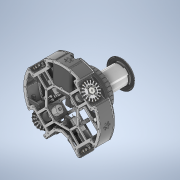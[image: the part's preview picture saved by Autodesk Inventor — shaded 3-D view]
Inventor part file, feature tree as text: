
AUTODESK INVENTOR PART (.ipt)
format: ipt  version: 2020 (Build 240168000, 168)  size: 43,642,880 bytes
history: native  units: mm
features: other x297, mirror x2
ambient origin geometry x8: Origin, YZ Plane, XZ Plane, XY Plane, X Axis, Y Axis, Z Axis, Center Point
bodies: Body1 (feature_tree), Body2 (feature_tree), Body3 (feature_tree), Body4 (feature_tree), Body5 (feature_tree), Body6 (feature_tree), Body7 (feature_tree), Body8 (feature_tree), Body9 (feature_tree), Body10 (feature_tree), Body11 (feature_tree), Body12 (feature_tree), Body13 (feature_tree), Body14 (feature_tree), Body15 (feature_tree), Body16 (feature_tree), Body17 (feature_tree), Body18 (feature_tree), Body19 (feature_tree), Body20 (feature_tree), Body21 (feature_tree), Body22 (feature_tree), Body23 (feature_tree), Body24 (feature_tree), Body25 (feature_tree), Body26 (feature_tree), Body27 (feature_tree), Body28 (feature_tree), Body29 (feature_tree), Body30 (feature_tree), Body31 (feature_tree), Body32 (feature_tree), Body33 (feature_tree), Body34 (feature_tree), Body35 (feature_tree), Body36 (feature_tree), Body37 (feature_tree), Body38 (feature_tree), Body39 (feature_tree), Body40 (feature_tree), Body41 (feature_tree), Body42 (feature_tree), Body43 (feature_tree), Body44 (feature_tree), Body45 (feature_tree), Body46 (feature_tree), Body47 (feature_tree), Body48 (feature_tree), Body49 (feature_tree), Body50 (feature_tree), Body51 (feature_tree), Body52 (feature_tree), Body53 (feature_tree), Body54 (feature_tree), Body55 (feature_tree), Body56 (feature_tree), Body57 (feature_tree), Body58 (feature_tree), Body59 (feature_tree), Body60 (feature_tree), Body61 (feature_tree), Body62 (feature_tree), Body63 (feature_tree), Body64 (feature_tree), Body65 (feature_tree), Body66 (feature_tree), Body67 (feature_tree), Body68 (feature_tree), Body69 (feature_tree), Body70 (feature_tree), Body71 (feature_tree), Body72 (feature_tree), Body73 (feature_tree), Body74 (feature_tree), Body75 (feature_tree), Body76 (feature_tree), Body77 (feature_tree), Body78 (feature_tree), Body79 (feature_tree), Body80 (feature_tree), Body81 (feature_tree), Body82 (feature_tree), Body83 (feature_tree), Body84 (feature_tree), Body85 (feature_tree), Body86 (feature_tree), Body87 (feature_tree), Body88 (feature_tree), Body89 (feature_tree), Body90 (feature_tree), Body91 (feature_tree), Body92 (feature_tree), Body93 (feature_tree), Body94 (feature_tree), Body95 (feature_tree), Body96 (feature_tree), Body97 (feature_tree), Body98 (feature_tree), Body99 (feature_tree), Body100 (feature_tree), Body101 (feature_tree), Body102 (feature_tree), Body103 (feature_tree), Body104 (feature_tree), Body105 (feature_tree), Body106 (feature_tree), Body107 (feature_tree), Body108 (feature_tree), Body109 (feature_tree), Body110 (feature_tree), Body111 (feature_tree), Body112 (feature_tree), Body113 (feature_tree), Body114 (feature_tree), Body115 (feature_tree), Body116 (feature_tree), Body117 (feature_tree), Body118 (feature_tree), Body119 (feature_tree), Body120 (feature_tree), Body121 (feature_tree), Body122 (feature_tree), Body123 (feature_tree), Body124 (feature_tree), Body125 (feature_tree), Body126 (feature_tree), Body127 (feature_tree), Body128 (feature_tree), Body129 (feature_tree), Body130 (feature_tree), Body131 (feature_tree), Body132 (feature_tree), Body133 (feature_tree), Body134 (feature_tree), Body135 (feature_tree), Body136 (feature_tree), Body137 (feature_tree), Body138 (feature_tree), Body139 (feature_tree), Body140 (feature_tree), Body141 (feature_tree), Body142 (feature_tree), Body143 (feature_tree), Body144 (feature_tree), Body145 (feature_tree), Body146 (feature_tree), Body147 (feature_tree), Body148 (feature_tree), Body149 (feature_tree), Body150 (feature_tree), Body151 (feature_tree), Body152 (feature_tree), Body153 (feature_tree), Body154 (feature_tree), Body155 (feature_tree), Body156 (feature_tree), Body157 (feature_tree), Body158 (feature_tree), Body159 (feature_tree), Body160 (feature_tree), Body161 (feature_tree), Body162 (feature_tree), Body163 (feature_tree), Body164 (feature_tree), Body165 (feature_tree), Body166 (feature_tree), Body167 (feature_tree), Body168 (feature_tree), Body169 (feature_tree), Body170 (feature_tree), Body171 (feature_tree), Body172 (feature_tree), Body173 (feature_tree), Body174 (feature_tree), Body175 (feature_tree), Body176 (feature_tree), Body177 (feature_tree), Body178 (feature_tree), Body179 (feature_tree), Body180 (feature_tree), Body181 (feature_tree), Body182 (feature_tree), Body183 (feature_tree), Body184 (feature_tree), Body185 (feature_tree), Body186 (feature_tree), Body187 (feature_tree), Body188 (feature_tree), Body189 (feature_tree), Body190 (feature_tree), Body191 (feature_tree), Body192 (feature_tree), Body193 (feature_tree), Body194 (feature_tree)
feature tree (299):
  other  "main2 render.iam"
  other  "bottom_plate.ipt:1"
  other  "back_motor_short.ipt:1"
  other  "back_motor_short.ipt:2"
  other  "upper_plate.ipt:1"
  other  "9Dof Razor IMU.ipt:1"
  other  "kicker_base_v6_wide.ipt:1"
  other  "kicker_head_flat_v4.ipt:1"
  other  "motor_body.ipt:1"
  other  "motor_body.ipt:2"
  other  "motor_body.ipt:3"
  other  "motor_body.ipt:4"
  other  "GTF Robots 50mm Wheel.ipt:1"
  other  "GTF Robots 50mm Wheel.ipt:2"
  other  "GTF Robots 50mm Wheel.ipt:3"
  other  "GTF Robots 50mm Wheel.ipt:4"
  other  "bat_bed003_clear.ipt:1"
  other  "right_motor_v2.ipt:1"
  other  "tsop_board_black.iam:1::Board.iam:1::Open CASCADE STEP translator 6.8 1.1.1.ipt:1"
  other  "tsop_board_black.iam:1::VCC.iam:1::cdled1608x06g.ipt:1"
  other  "tsop_board_black.iam:1::XP1.iam:1::5822834224.ipt:1"
  other  "tsop_board_black.iam:1::TS32.iam:1::TSOP.ipt:1"
  other  "tsop_board_black.iam:1::TS31.iam:1::TSOP.ipt:1"
  other  "tsop_board_black.iam:1::TS30.iam:1::TSOP.ipt:1"
  other  "tsop_board_black.iam:1::TS29.iam:1::TSOP.ipt:1"
  other  "tsop_board_black.iam:1::TS28.iam:1::TSOP.ipt:1"
  other  "tsop_board_black.iam:1::TS27.iam:1::TSOP.ipt:1"
  other  "tsop_board_black.iam:1::TS26.iam:1::TSOP.ipt:1"
  other  "tsop_board_black.iam:1::TS25.iam:1::TSOP.ipt:1"
  other  "tsop_board_black.iam:1::TS24.iam:1::TSOP.ipt:1"
  other  "tsop_board_black.iam:1::TS23.iam:1::TSOP.ipt:1"
  other  "tsop_board_black.iam:1::TS22.iam:1::TSOP.ipt:1"
  other  "tsop_board_black.iam:1::TS21.iam:1::TSOP.ipt:1"
  other  "tsop_board_black.iam:1::TS20.iam:1::TSOP.ipt:1"
  other  "tsop_board_black.iam:1::TS19.iam:1::TSOP.ipt:1"
  other  "tsop_board_black.iam:1::TS18.iam:1::TSOP.ipt:1"
  other  "tsop_board_black.iam:1::TS17.iam:1::TSOP.ipt:1"
  other  "tsop_board_black.iam:1::TS16.iam:1::TSOP.ipt:1"
  other  "tsop_board_black.iam:1::TS15.iam:1::TSOP.ipt:1"
  other  "tsop_board_black.iam:1::TS14.iam:1::TSOP.ipt:1"
  other  "tsop_board_black.iam:1::TS13.iam:1::TSOP.ipt:1"
  other  "tsop_board_black.iam:1::TS12.iam:1::TSOP.ipt:1"
  other  "tsop_board_black.iam:1::TS11.iam:1::TSOP.ipt:1"
  other  "tsop_board_black.iam:1::TS10.iam:1::TSOP.ipt:1"
  other  "tsop_board_black.iam:1::TS9.iam:1::TSOP.ipt:1"
  other  "tsop_board_black.iam:1::TS8.iam:1::TSOP.ipt:1"
  other  "tsop_board_black.iam:1::TS7.iam:1::TSOP.ipt:1"
  other  "tsop_board_black.iam:1::TS6.iam:1::TSOP.ipt:1"
  other  "tsop_board_black.iam:1::TS5.iam:1::TSOP.ipt:1"
  other  "tsop_board_black.iam:1::TS4.iam:1::TSOP.ipt:1"
  other  "tsop_board_black.iam:1::TS3.iam:1::TSOP.ipt:1"
  other  "tsop_board_black.iam:1::TS2.iam:1::TSOP.ipt:1"
  other  "tsop_board_black.iam:1::TS1.iam:1::TSOP.ipt:1"
  other  "tsop_board_black.iam:1::R33.iam:1::RES0805.ipt:1"
  other  "tsop_board_black.iam:1::MUX2.iam:1::CD74HC4067SM96--3DModel-STEP-56544.ipt:1"
  other  "tsop_board_black.iam:1::MUX1.iam:1::CD74HC4067SM96--3DModel-STEP-56544.ipt:1"
  other  "tsop_board_black.iam:1::C35.iam:1::C0805D(I).ipt:1"
  other  "tsop_board_black.iam:1::C34.iam:1::C0805D(I).ipt:1"
  other  "tsop_board_black.iam:1::C33.iam:1::C0805D(I).ipt:1"
  other  "tsop_board_black.iam:1::C32.iam:1::C0805D(I).ipt:1"
  other  "tsop_board_black.iam:1::C31.iam:1::C0805D(I).ipt:1"
  other  "tsop_board_black.iam:1::C30.iam:1::C0805D(I).ipt:1"
  other  "tsop_board_black.iam:1::C28.iam:1::C0805D(I).ipt:1"
  other  "tsop_board_black.iam:1::C27.iam:1::C0805D(I).ipt:1"
  other  "tsop_board_black.iam:1::C26.iam:1::C0805D(I).ipt:1"
  other  "tsop_board_black.iam:1::C25.iam:1::C0805D(I).ipt:1"
  other  "tsop_board_black.iam:1::C24.iam:1::C0805D(I).ipt:1"
  other  "tsop_board_black.iam:1::C23.iam:1::C0805D(I).ipt:1"
  other  "tsop_board_black.iam:1::C22.iam:1::C0805D(I).ipt:1"
  other  "tsop_board_black.iam:1::C21.iam:1::C0805D(I).ipt:1"
  other  "tsop_board_black.iam:1::C20.iam:1::C0805D(I).ipt:1"
  other  "tsop_board_black.iam:1::C19.iam:1::C0805D(I).ipt:1"
  other  "tsop_board_black.iam:1::C18.iam:1::C0805D(I).ipt:1"
  other  "tsop_board_black.iam:1::C17.iam:1::C0805D(I).ipt:1"
  other  "tsop_board_black.iam:1::C16.iam:1::C0805D(I).ipt:1"
  other  "tsop_board_black.iam:1::C15.iam:1::C0805D(I).ipt:1"
  other  "tsop_board_black.iam:1::C14.iam:1::C0805D(I).ipt:1"
  other  "tsop_board_black.iam:1::C12.iam:1::C0805D(I).ipt:1"
  other  "tsop_board_black.iam:1::C11.iam:1::C0805D(I).ipt:1"
  other  "tsop_board_black.iam:1::C10.iam:1::C0805D(I).ipt:1"
  other  "tsop_board_black.iam:1::C9.iam:1::C0805D(I).ipt:1"
  other  "tsop_board_black.iam:1::C8.iam:1::C0805D(I).ipt:1"
  other  "tsop_board_black.iam:1::C7.iam:1::C0805D(I).ipt:1"
  other  "tsop_board_black.iam:1::C6.iam:1::C0805D(I).ipt:1"
  other  "tsop_board_black.iam:1::C5.iam:1::C0805D(I).ipt:1"
  other  "tsop_board_black.iam:1::C4.iam:1::C0805D(I).ipt:1"
  other  "tsop_board_black.iam:1::C3.iam:1::C0805D(I).ipt:1"
  other  "tsop_board_black.iam:1::C2.iam:1::C0805D(I).ipt:1"
  other  "tsop_board_black.iam:1::C1.iam:1::C0805D(I).ipt:1"
  mirror  "mirror_50.ipt:1"
  other  "tube_50.ipt:1"
  mirror  "mirror_lock_v4.ipt:1"
  other  "board_support.ipt:1"
  other  "tsop_imu_v1.ipt:1"
  other  "tsop_mount_v4.ipt:1"
  other  "side_prot.ipt:2"
  other  "motherboard.ipt:1"
  other  "optic_mount_v3.ipt:1"
  other  "side_prot_stab_60.ipt:1"
  other  "mid_mount_v3.ipt:1"
  other  "mid_mount_v3.ipt:2"
  other  "mid_mount_v3.ipt:3"
  other  "mid_mount_v3.ipt:4"
  other  "bat_case_v6.ipt:1"
  other  "left_motor_v3.ipt:1"
  other  "Твердое тело1"
  other  "Твердое тело2"
  other  "Твердое тело3"
  other  "Твердое тело4"
  other  "Твердое тело5"
  other  "Твердое тело6"
  other  "Твердое тело7"
  other  "Твердое тело8"
  other  "Твердое тело9"
  other  "Твердое тело10"
  other  "Твердое тело11"
  other  "Твердое тело12"
  other  "Твердое тело13"
  other  "Твердое тело14"
  other  "Твердое тело15"
  other  "Твердое тело16"
  other  "Твердое тело17"
  other  "Твердое тело18"
  other  "Твердое тело19"
  other  "Твердое тело20"
  other  "Твердое тело21"
  other  "Твердое тело22"
  other  "Твердое тело23"
  other  "Твердое тело24"
  other  "Твердое тело25"
  other  "Твердое тело26"
  other  "Твердое тело27"
  other  "Твердое тело28"
  other  "Твердое тело29"
  other  "Твердое тело30"
  other  "Твердое тело31"
  other  "Твердое тело32"
  other  "Твердое тело33"
  other  "Твердое тело34"
  other  "Твердое тело35"
  other  "Твердое тело36"
  other  "Твердое тело37"
  other  "Твердое тело38"
  other  "Твердое тело39"
  other  "Твердое тело40"
  other  "Твердое тело41"
  other  "Твердое тело42"
  other  "Твердое тело43"
  other  "Твердое тело44"
  other  "Твердое тело45"
  other  "Твердое тело46"
  other  "Твердое тело47"
  other  "Твердое тело48"
  other  "Твердое тело49"
  other  "Твердое тело50"
  other  "Твердое тело51"
  other  "Твердое тело52"
  other  "Твердое тело53"
  other  "Твердое тело54"
  other  "Твердое тело55"
  other  "Твердое тело56"
  other  "Твердое тело57"
  other  "Твердое тело58"
  other  "Твердое тело59"
  other  "Твердое тело60"
  other  "Твердое тело61"
  other  "Твердое тело62"
  other  "Твердое тело63"
  other  "Твердое тело64"
  other  "Твердое тело65"
  other  "Твердое тело66"
  other  "Твердое тело67"
  other  "Твердое тело68"
  other  "Твердое тело69"
  other  "Твердое тело70"
  other  "Твердое тело71"
  other  "Твердое тело72"
  other  "Твердое тело73"
  other  "Твердое тело74"
  other  "Твердое тело75"
  other  "Твердое тело76"
  other  "Твердое тело77"
  other  "Твердое тело78"
  other  "Твердое тело79"
  other  "Твердое тело80"
  other  "Твердое тело81"
  other  "Твердое тело82"
  other  "Твердое тело83"
  other  "Твердое тело84"
  other  "Твердое тело85"
  other  "Твердое тело86"
  other  "Твердое тело87"
  other  "Твердое тело88"
  other  "Твердое тело89"
  other  "Твердое тело90"
  other  "Твердое тело91"
  other  "Твердое тело92"
  other  "Твердое тело93"
  other  "Твердое тело94"
  other  "Твердое тело95"
  other  "Твердое тело96"
  other  "Твердое тело97"
  other  "Твердое тело98"
  other  "Твердое тело99"
  other  "Твердое тело100"
  other  "Твердое тело101"
  other  "Твердое тело102"
  other  "Твердое тело103"
  other  "Твердое тело104"
  other  "Твердое тело105"
  other  "Твердое тело106"
  other  "Твердое тело107"
  other  "Твердое тело108"
  other  "Твердое тело109"
  other  "Твердое тело110"
  other  "Твердое тело111"
  other  "Твердое тело112"
  other  "Твердое тело113"
  other  "Твердое тело114"
  other  "Твердое тело115"
  other  "Твердое тело116"
  other  "Твердое тело117"
  other  "Твердое тело118"
  other  "Твердое тело119"
  other  "Твердое тело120"
  other  "Твердое тело121"
  other  "Твердое тело122"
  other  "Твердое тело123"
  other  "Твердое тело124"
  other  "Твердое тело125"
  other  "Твердое тело126"
  other  "Твердое тело127"
  other  "Твердое тело128"
  other  "Твердое тело129"
  other  "Твердое тело130"
  other  "Твердое тело131"
  other  "Твердое тело132"
  other  "Твердое тело133"
  other  "Твердое тело134"
  other  "Твердое тело135"
  other  "Твердое тело136"
  other  "Твердое тело137"
  other  "Твердое тело138"
  other  "Твердое тело139"
  other  "Твердое тело140"
  other  "Твердое тело141"
  other  "Твердое тело142"
  other  "Твердое тело143"
  other  "Твердое тело144"
  other  "Твердое тело145"
  other  "Твердое тело146"
  other  "Твердое тело147"
  other  "Твердое тело148"
  other  "Твердое тело149"
  other  "Твердое тело150"
  other  "Твердое тело151"
  other  "Твердое тело152"
  other  "Твердое тело153"
  other  "Твердое тело154"
  other  "Твердое тело155"
  other  "Твердое тело156"
  other  "Твердое тело157"
  other  "Твердое тело158"
  other  "Твердое тело159"
  other  "Твердое тело160"
  other  "Твердое тело161"
  other  "Твердое тело162"
  other  "Твердое тело163"
  other  "Твердое тело164"
  other  "Твердое тело165"
  other  "Твердое тело166"
  other  "Твердое тело167"
  other  "Твердое тело168"
  other  "Твердое тело169"
  other  "Твердое тело170"
  other  "Твердое тело171"
  other  "Твердое тело172"
  other  "Твердое тело173"
  other  "Твердое тело174"
  other  "Твердое тело175"
  other  "Твердое тело176"
  other  "Твердое тело177"
  other  "Твердое тело178"
  other  "Твердое тело179"
  other  "Твердое тело180"
  other  "Твердое тело181"
  other  "Твердое тело182"
  other  "Твердое тело183"
  other  "Твердое тело184"
  other  "Твердое тело185"
  other  "Твердое тело186"
  other  "Твердое тело187"
  other  "Твердое тело188"
  other  "Твердое тело189"
  other  "Твердое тело190"
  other  "Твердое тело191"
  other  "Твердое тело192"
  other  "Твердое тело193"
  other  "Твердое тело194"
